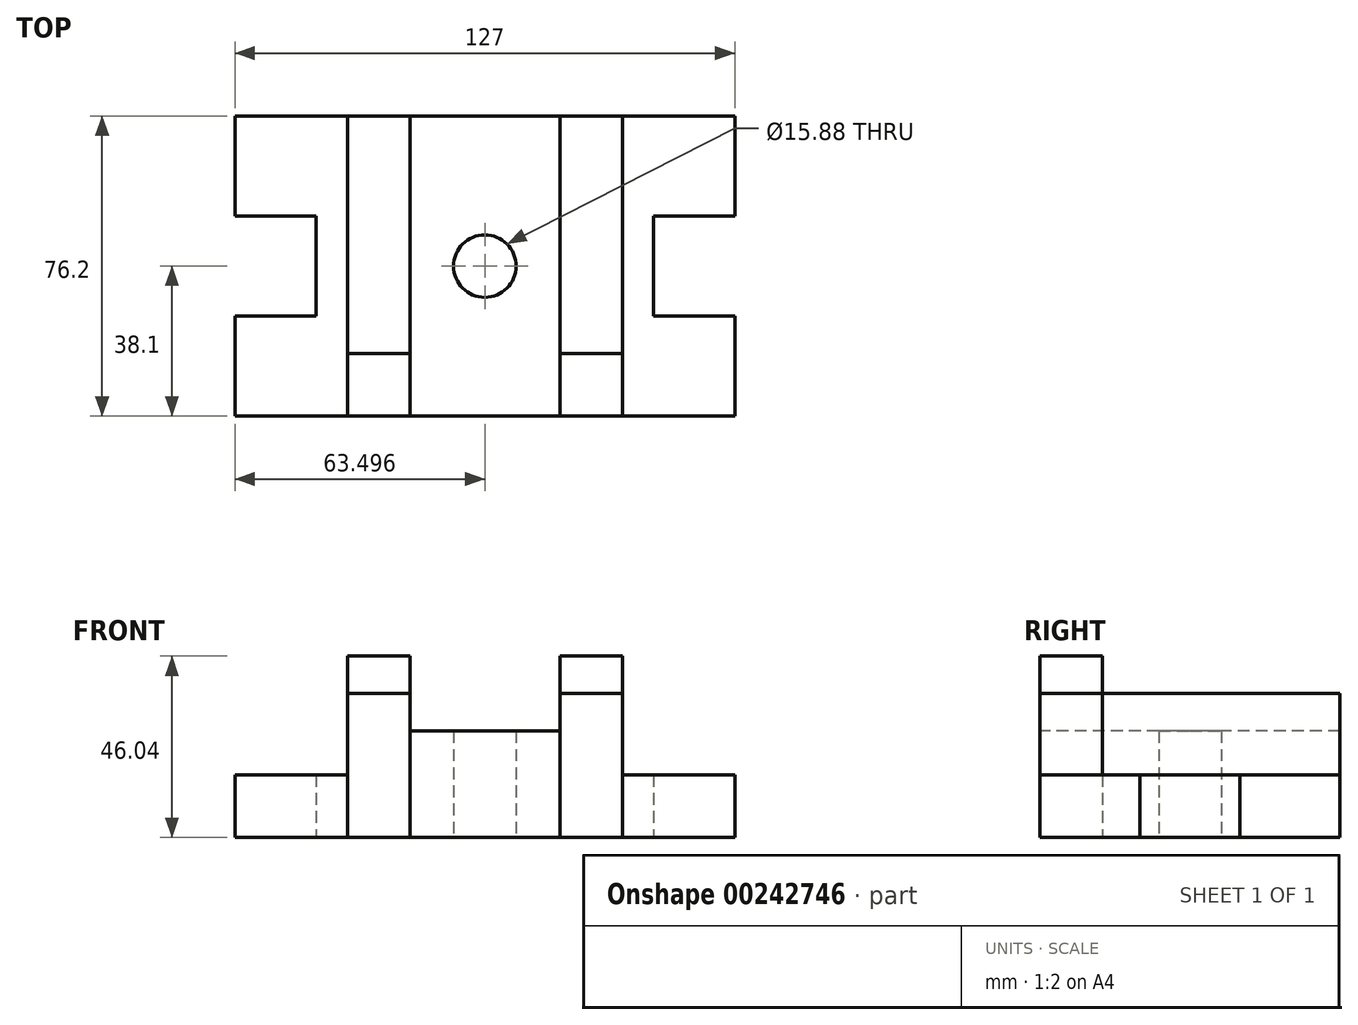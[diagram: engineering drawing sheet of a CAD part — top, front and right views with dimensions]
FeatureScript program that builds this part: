
annotation { "Feature Type Name" : "Feature", "Feature Type Description" : "" }
export const myFeature = defineFeature(function(context is Context, id is Id, definition is map)
    precondition{}
    {
        {
            var Q0;
            Q0=qCreatedBy(makeId("Top.planeOp"),FACE);
            var sketch = newSketch(context, id + "F0", { "sketchPlane" : qUnion([Q0])});
            skLineSegment(sketch, "E0.bottom", {"start": v(-109.07, 76.2) * mm, "end": v(144.93, 76.2) * mm});
            skLineSegment(sketch, "E0.top", {"start": v(-109.07, -76.2) * mm, "end": v(144.93, -76.2) * mm});
            skLineSegment(sketch, "E0.left", {"start": v(-109.07, 76.2) * mm, "end": v(-109.07, -76.2) * mm});
            skLineSegment(sketch, "E0.right", {"start": v(144.93, 76.2) * mm, "end": v(144.93, -76.2) * mm});
            skLineSegment(sketch, "E1.bottom", {"start": v(103.66, 25.4) * mm, "end": v(144.93, 25.4) * mm});
            skLineSegment(sketch, "E1.top", {"start": v(103.66, -25.4) * mm, "end": v(144.93, -25.4) * mm});
            skLineSegment(sketch, "E1.left", {"start": v(103.66, 25.4) * mm, "end": v(103.66, -25.4) * mm});
            skLineSegment(sketch, "E1.right", {"start": v(144.93, 25.4) * mm, "end": v(144.93, -25.4) * mm});
            skLineSegment(sketch, "E2.bottom", {"start": v(-109.07, 25.4) * mm, "end": v(-67.8, 25.4) * mm});
            skLineSegment(sketch, "E2.top", {"start": v(-109.07, -25.4) * mm, "end": v(-67.8, -25.4) * mm});
            skLineSegment(sketch, "E2.left", {"start": v(-109.07, 25.4) * mm, "end": v(-109.07, -25.4) * mm});
            skLineSegment(sketch, "E2.right", {"start": v(-67.8, 25.4) * mm, "end": v(-67.8, -25.4) * mm});
            skLineSegment(sketch, "E3.bottom", {"start": v(-51.92, 76.2) * mm, "end": v(-20.17, 76.2) * mm});
            skLineSegment(sketch, "E3.top", {"start": v(-51.92, -76.2) * mm, "end": v(-20.17, -76.2) * mm});
            skLineSegment(sketch, "E3.left", {"start": v(-51.92, 76.2) * mm, "end": v(-51.92, -76.2) * mm});
            skLineSegment(sketch, "E3.right", {"start": v(-20.17, 76.2) * mm, "end": v(-20.17, -76.2) * mm});
            skLineSegment(sketch, "E4.bottom", {"start": v(56.03, 76.2) * mm, "end": v(87.78, 76.2) * mm});
            skLineSegment(sketch, "E4.top", {"start": v(56.03, -76.2) * mm, "end": v(87.78, -76.2) * mm});
            skLineSegment(sketch, "E4.left", {"start": v(56.03, 76.2) * mm, "end": v(56.03, -76.2) * mm});
            skLineSegment(sketch, "E4.right", {"start": v(87.78, 76.2) * mm, "end": v(87.78, -76.2) * mm});
            skLineSegment(sketch, "E5.top", {"start": v(-51.92, 44.45) * mm, "end": v(-20.17, 44.45) * mm});
            skLineSegment(sketch, "E5.left", {"start": v(-51.92, 76.2) * mm, "end": v(-51.92, 44.45) * mm});
            skLineSegment(sketch, "E5.right", {"start": v(-20.17, 76.2) * mm, "end": v(-20.17, 44.45) * mm});
            skLineSegment(sketch, "E6.bottom", {"start": v(-51.92, -44.45) * mm, "end": v(-20.17, -44.45) * mm});
            skLineSegment(sketch, "E6.left", {"start": v(-51.92, -44.45) * mm, "end": v(-51.92, -76.2) * mm});
            skLineSegment(sketch, "E6.right", {"start": v(-20.17, -44.45) * mm, "end": v(-20.17, -76.2) * mm});
            skLineSegment(sketch, "E7.top", {"start": v(56.03, 44.45) * mm, "end": v(87.78, 44.45) * mm});
            skLineSegment(sketch, "E7.left", {"start": v(56.03, 76.2) * mm, "end": v(56.03, 44.45) * mm});
            skLineSegment(sketch, "E7.right", {"start": v(87.78, 76.2) * mm, "end": v(87.78, 44.45) * mm});
            skLineSegment(sketch, "E8.bottom", {"start": v(56.03, -44.45) * mm, "end": v(87.78, -44.45) * mm});
            skLineSegment(sketch, "E8.left", {"start": v(56.03, -44.45) * mm, "end": v(56.03, -76.2) * mm});
            skLineSegment(sketch, "E8.right", {"start": v(87.78, -44.45) * mm, "end": v(87.78, -76.2) * mm});
            skCircle(sketch, "E9", {"center": v(17.93, 0) * mm, "radius": 15.88 * mm});
            skSolve(sketch);
        }
        {
            var Q0;
            {var subQ5=sQuery(id+"F0.wireOp",EDGE,"E2.bottom");Q0=makeQuery(id+"F0.imprint","IMPRINT",FACE,{"disambiguationData":[TD([[makeQuery(id+"F0.imprint","IMPRINT",EDGE,{"derivedFrom":subQ5}),1.0]])]});}
            extrude(context, id + "F1", {"entities" : qUnion([Q0]), "depth" : 31.75 * mm});
        }
        {
            var Q0;
            {var subQ8=sQuery(id+"F0.wireOp",EDGE,"E1.bottom");Q0=makeQuery(id+"F0.imprint","IMPRINT",FACE,{"disambiguationData":[TD([[makeQuery(id+"F0.imprint","IMPRINT",EDGE,{"derivedFrom":subQ8}),1.0]])]});}
            extrude(context, id + "F2", {"entities" : qUnion([Q0]), "depth" : 31.75 * mm});
        }
        {
            var Q0;
            Q0=makeQuery(id+"F0.imprint","IMPRINT",FACE,{"disambiguationData":[TD([[makeQuery(id+"F0.imprint","IMPRINT",EDGE,{"derivedFrom":sQuery(id+"F0.wireOp",EDGE,"E6.bottom")}),-1.0]])]});
            var Q1;
            Q1=makeQuery(id+"F0.imprint","IMPRINT",FACE,{"disambiguationData":[TD([[makeQuery(id+"F0.imprint","IMPRINT",EDGE,{"derivedFrom":sQuery(id+"F0.wireOp",EDGE,"E3.bottom")}),-1.0]])]});
            var Q2;
            Q2=makeQuery(id+"F0.imprint","IMPRINT",FACE,{"disambiguationData":[TD([[makeQuery(id+"F0.imprint","IMPRINT",EDGE,{"derivedFrom":sQuery(id+"F0.wireOp",EDGE,"E4.bottom")}),-1.0]])]});
            var Q3;
            Q3=makeQuery(id+"F0.imprint","IMPRINT",FACE,{"disambiguationData":[TD([[makeQuery(id+"F0.imprint","IMPRINT",EDGE,{"derivedFrom":sQuery(id+"F0.wireOp",EDGE,"E8.bottom")}),-1.0]])]});
            extrude(context, id + "F3", {"entities" : qUnion([Q0, Q1, Q2, Q3]), "depth" : 92.07 * mm});
        }
        {
            var Q0;
            Q0=makeQuery(id+"F0.imprint","IMPRINT",FACE,{"disambiguationData":[TD([[makeQuery(id+"F0.imprint","IMPRINT",EDGE,{"derivedFrom":sQuery(id+"F0.wireOp",EDGE,"E3.left")}),1.0]])]});
            var Q1;
            Q1=makeQuery(id+"F0.imprint","IMPRINT",FACE,{"disambiguationData":[TD([[makeQuery(id+"F0.imprint","IMPRINT",EDGE,{"derivedFrom":sQuery(id+"F0.wireOp",EDGE,"E4.left")}),1.0]])]});
            extrude(context, id + "F4", {"entities" : qUnion([Q0, Q1]), "depth" : 73.02 * mm});
        }
        {
            var Q0;
            Q0=makeQuery(id+"F0.imprint","IMPRINT",FACE,{"disambiguationData":[TD([[makeQuery(id+"F0.imprint","IMPRINT",EDGE,{"derivedFrom":sQuery(id+"F0.wireOp",EDGE,"E3.right")}),1.0]])]});
            extrude(context, id + "F5", {"entities" : qUnion([Q0]), "depth" : 53.97 * mm});
        }
        {
            var Q0;
            Q0=makeQuery(id+"F1.opExtrude","SWEPT_BODY",BODY,{"disambiguationData":[OSD([sQuery(id+"F0.wireOp",EDGE,"E0.bottom"),sQuery(id+"F0.wireOp",EDGE,"E0.top"),sQuery(id+"F0.wireOp",EDGE,"E0.left"),sQuery(id+"F0.wireOp",EDGE,"E2.bottom"),sQuery(id+"F0.wireOp",EDGE,"E2.top"),sQuery(id+"F0.wireOp",EDGE,"E2.right"),sQuery(id+"F0.wireOp",EDGE,"E3.left"),sQuery(id+"F0.wireOp",EDGE,"E5.left"),sQuery(id+"F0.wireOp",EDGE,"E6.left")])]});
            var Q1;
            Q1=makeQuery(id+"F2.opExtrude","SWEPT_BODY",BODY,{"disambiguationData":[OSD([sQuery(id+"F0.wireOp",EDGE,"E0.bottom"),sQuery(id+"F0.wireOp",EDGE,"E0.top"),sQuery(id+"F0.wireOp",EDGE,"E0.right"),sQuery(id+"F0.wireOp",EDGE,"E1.bottom"),sQuery(id+"F0.wireOp",EDGE,"E1.top"),sQuery(id+"F0.wireOp",EDGE,"E1.left"),sQuery(id+"F0.wireOp",EDGE,"E4.right"),sQuery(id+"F0.wireOp",EDGE,"E7.right"),sQuery(id+"F0.wireOp",EDGE,"E8.right")])]});
            var Q2;
            Q2=makeQuery(id+"F3.opExtrude","SWEPT_BODY",BODY,{"disambiguationData":[OSD([sQuery(id+"F0.wireOp",EDGE,"E3.bottom"),sQuery(id+"F0.wireOp",EDGE,"E5.top"),sQuery(id+"F0.wireOp",EDGE,"E5.left"),sQuery(id+"F0.wireOp",EDGE,"E5.right")])]});
            var Q3;
            Q3=makeQuery(id+"F3.opExtrude","SWEPT_BODY",BODY,{"disambiguationData":[OSD([sQuery(id+"F0.wireOp",EDGE,"E6.bottom"),sQuery(id+"F0.wireOp",EDGE,"E3.top"),sQuery(id+"F0.wireOp",EDGE,"E6.left"),sQuery(id+"F0.wireOp",EDGE,"E6.right")])]});
            var Q4;
            Q4=makeQuery(id+"F3.opExtrude","SWEPT_BODY",BODY,{"disambiguationData":[OSD([sQuery(id+"F0.wireOp",EDGE,"E4.bottom"),sQuery(id+"F0.wireOp",EDGE,"E7.top"),sQuery(id+"F0.wireOp",EDGE,"E7.left"),sQuery(id+"F0.wireOp",EDGE,"E7.right")])]});
            var Q5;
            Q5=makeQuery(id+"F3.opExtrude","SWEPT_BODY",BODY,{"disambiguationData":[OSD([sQuery(id+"F0.wireOp",EDGE,"E8.bottom"),sQuery(id+"F0.wireOp",EDGE,"E4.top"),sQuery(id+"F0.wireOp",EDGE,"E8.left"),sQuery(id+"F0.wireOp",EDGE,"E8.right")])]});
            var Q6;
            Q6=makeQuery(id+"F4.opExtrude","SWEPT_BODY",BODY,{"disambiguationData":[OSD([sQuery(id+"F0.wireOp",EDGE,"E3.left"),sQuery(id+"F0.wireOp",EDGE,"E3.right"),sQuery(id+"F0.wireOp",EDGE,"E5.top"),sQuery(id+"F0.wireOp",EDGE,"E6.bottom")])]});
            var Q7;
            Q7=makeQuery(id+"F4.opExtrude","SWEPT_BODY",BODY,{"disambiguationData":[OSD([sQuery(id+"F0.wireOp",EDGE,"E4.left"),sQuery(id+"F0.wireOp",EDGE,"E4.right"),sQuery(id+"F0.wireOp",EDGE,"E7.top"),sQuery(id+"F0.wireOp",EDGE,"E8.bottom")])]});
            var Q8;
            Q8=makeQuery(id+"F5.opExtrude","SWEPT_BODY",BODY,{"disambiguationData":[OSD([sQuery(id+"F0.wireOp",EDGE,"E0.bottom"),sQuery(id+"F0.wireOp",EDGE,"E0.top"),sQuery(id+"F0.wireOp",EDGE,"E3.right"),sQuery(id+"F0.wireOp",EDGE,"E4.left"),sQuery(id+"F0.wireOp",EDGE,"E5.right"),sQuery(id+"F0.wireOp",EDGE,"E6.right"),sQuery(id+"F0.wireOp",EDGE,"E7.left"),sQuery(id+"F0.wireOp",EDGE,"E8.left"),sQuery(id+"F0.wireOp",EDGE,"E9")])]});
            var Q9;
            Q9=qCreatedBy(makeId("Origin.pointOp"),VERTEX);
            transform(context, id + "F6", {"entities" : qUnion([Q0, Q1, Q2, Q3, Q4, Q5, Q6, Q7, Q8]), "transformType" : TransformType.SCALE_UNIFORMLY, "scale" : 0.5, "scalePoint" : qUnion([Q9]), "makeCopy" : false});
        }
    });
